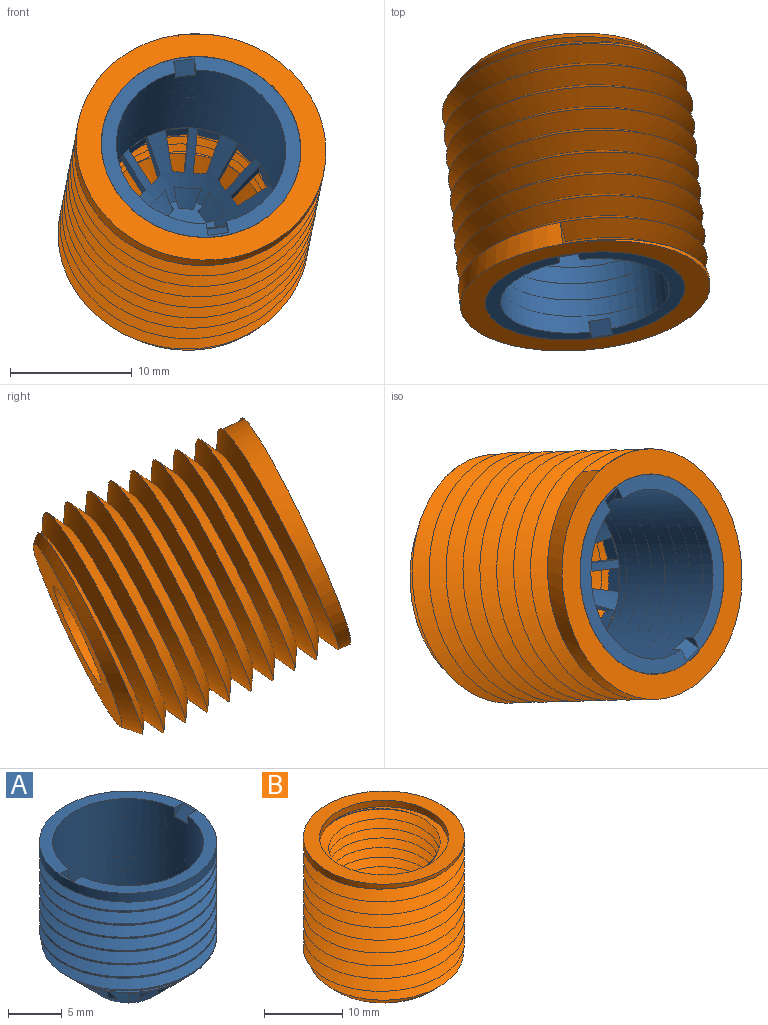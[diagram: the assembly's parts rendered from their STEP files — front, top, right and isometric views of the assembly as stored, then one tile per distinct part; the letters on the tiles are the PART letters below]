
ASSEMBLY  parts=2 mates=1
PART A: 152 faces, bbox 17.6x20.2x19.9 mm
  f0: cylinder r=7mm len=14mm, axis (0,0,1), area 481.2mm2, adj f1,f3,f4,f6,f7,f65,f66,f67
  f1: plane 1.75x0.06mm, normal (0,0,1), area 0mm2, adj f0,f2,f3,f151
  f2: plane 1.75x1mm, normal (0.71,0,0.71), area 2.5mm2, adj f1,f3,f150,f151
  f3: plane 1.06x1mm, normal (0,1,0), area 0.6mm2, adj f0,f1,f2,f150
  f4: plane 1.06x1mm, normal (0,1,0), area 0.6mm2, adj f0,f5,f148,f150
  f5: plane 1.75x1mm, normal (-0.71,0,0.71), area 2.5mm2, adj f4,f148,f149,f150
  f6: cone r=7mm half-angle=45deg, axis (0,0,1), area 0mm2, adj f0,f7
  f7: plane 2.15x1.49mm, normal (-1,0.04,0), area 2.4mm2, adj f0,f6,f8,f65,f66,f146,f147
  f8: cone r=8.23mm half-angle=45deg, axis (0,0,1), area 142mm2, adj f7,f9,f10,f11,f12,f13,f14,f15
  f9: plane 1.54x0.95mm, normal (0.78,0.62,0), area 1.3mm2, adj f8,f133,f138,f145
  f10: plane 1.54x0.96mm, normal (0.78,0.62,0), area 1.3mm2, adj f8,f139,f144,f145
  f11: plane 1.54x0.95mm, normal (-0.78,0.62,0), area 1.3mm2, adj f8,f109,f114,f145
  f12: plane 1.54x1.16mm, normal (-0.97,-0.22,0), area 1.3mm2, adj f8,f103,f108,f145
  f13: plane 1.54x1.17mm, normal (-0.97,-0.22,0), area 1.3mm2, adj f8,f97,f102,f145
  f14: plane 1.54x1.19mm, normal (0,1,0), area 1.3mm2, adj f8,f127,f132,f145
  f15: plane 1.54x1.19mm, normal (0,1,0), area 1.3mm2, adj f8,f121,f126,f145
  f16: plane 1.54x0.96mm, normal (-0.78,0.62,0), area 1.3mm2, adj f8,f115,f120,f145
  f17: plane 1.54x1.08mm, normal (0.43,-0.9,0), area 1.3mm2, adj f8,f73,f78,f145
  f18: plane 1.54x1.08mm, normal (0.43,-0.9,0), area 1.3mm2, adj f8,f79,f84,f145
  f19: plane 1.54x1.16mm, normal (0.97,-0.22,0), area 1.3mm2, adj f8,f67,f72,f145
  f20: plane 1.54x1.08mm, normal (-0.43,-0.9,0), area 1.3mm2, adj f8,f91,f96,f145
  f21: plane 1.54x1.08mm, normal (-0.43,-0.9,0), area 1.3mm2, adj f8,f85,f90,f145
  f22: plane 1.57x1.41mm, normal (-0.99,0.12,0), area 1.2mm2, adj f8,f23,f24,f31,f32,f61
  f23: plane 1.09x0.52mm, normal (-0.43,-0.9,0), area 0.6mm2, adj f22,f24,f33,f61
  f24: plane 4.97x4.86mm, normal (0,0,1), area 12.5mm2, adj f22,f23,f25,f26,f27,f28,f29,f30
  f25: plane 1.17x0.48mm, normal (-0.97,-0.22,0), area 0.6mm2, adj f24,f34,f36,f61
  f26: plane 0.94x0.75mm, normal (-0.78,0.62,0), area 0.6mm2, adj f24,f37,f39,f61
  f27: plane 1.2x0.48mm, normal (0,1,0), area 0.6mm2, adj f24,f40,f42,f61
  f28: plane 0.94x0.75mm, normal (0.78,0.62,0), area 0.6mm2, adj f24,f43,f45,f61
  f29: plane 1.17x0.48mm, normal (0.97,-0.22,0), area 0.6mm2, adj f24,f46,f60,f61
  f30: plane 1.09x0.52mm, normal (0.43,-0.9,0), area 0.6mm2, adj f24,f61,f62,f64
  f31: cone r=7mm half-angle=45deg, axis (0,0,1), area 45.9mm2, adj f22,f24,f32,f33,f34,f35,f36,f37
  f32: plane 2.54x1.93mm, normal (0.43,0.9,0), area 2.7mm2, adj f8,f22,f31,f33
  f33: plane 1.41x1.12mm, normal (0.71,-0.7,0), area 1.2mm2, adj f8,f23,f24,f31,f32,f61
  f34: plane 1.41x1.34mm, normal (-0.53,0.85,0), area 1.2mm2, adj f8,f24,f25,f31,f35,f61
  f35: plane 2.7x1.93mm, normal (0.97,0.22,0), area 2.7mm2, adj f8,f31,f34,f36
  f36: plane 1.57x1.41mm, normal (-0.11,-0.99,0), area 1.2mm2, adj f8,f24,f25,f31,f35,f61
  f37: plane 1.49x1.41mm, normal (0.34,0.94,0), area 1.2mm2, adj f8,f24,f26,f31,f38,f61
  f38: plane 2.27x1.93mm, normal (0.78,-0.62,0), area 2.7mm2, adj f8,f31,f37,f39
  f39: plane 1.41x1.33mm, normal (-0.84,-0.54,0), area 1.2mm2, adj f8,f24,f26,f31,f38,f61
  f40: plane 1.49x1.41mm, normal (0.95,0.32,0), area 1.2mm2, adj f8,f24,f27,f31,f41,f61
  f41: plane 2.76x1.93mm, normal (0,-1,0), area 2.7mm2, adj f8,f31,f40,f42
  f42: plane 1.49x1.41mm, normal (-0.95,0.32,0), area 1.2mm2, adj f8,f24,f27,f31,f41,f61
  f43: plane 1.41x1.33mm, normal (0.84,-0.54,0), area 1.2mm2, adj f8,f24,f28,f31,f44,f61
  f44: plane 2.27x1.93mm, normal (-0.78,-0.62,0), area 2.7mm2, adj f8,f31,f43,f45
  f45: plane 1.49x1.41mm, normal (-0.34,0.94,0), area 1.2mm2, adj f8,f24,f28,f31,f44,f61
  f46: plane 1.57x1.41mm, normal (0.11,-0.99,0), area 1.2mm2, adj f8,f24,f29,f31,f59,f61
  f47: cylinder r=8.23mm len=14.47mm, axis (0,0,1), area 4.7mm2, adj f8,f48,f56,f57
  f48: cylinder r=8.23mm len=16.46mm, axis (0,0,1), area 8.6mm2, adj f47,f49,f56,f57
  f49: cylinder r=8.23mm len=16.46mm, axis (0,0,1), area 8.6mm2, adj f48,f50,f56,f57
  f50: cylinder r=8.23mm len=16.46mm, axis (0,0,1), area 8.6mm2, adj f49,f51,f56,f57
  f51: cylinder r=8.23mm len=16.46mm, axis (0,0,1), area 8.6mm2, adj f50,f52,f56,f57
  f52: cylinder r=8.23mm len=16.46mm, axis (0,0,1), area 8.6mm2, adj f51,f53,f56,f57
  f53: cylinder r=8.23mm len=16.46mm, axis (0,0,1), area 8.6mm2, adj f52,f54,f56,f57
  f54: cylinder r=8.23mm len=16.46mm, axis (0,0,1), area 54.6mm2, adj f53,f55,f56,f57,f150
  f55: plane 17.38x17.38mm, normal (0,0,-1), area 25.3mm2, adj f54,f56,f57
  f56: bspline ~19.24x16.66mm, area 308mm2, adj f8,f47,f48,f49,f50,f51,f52,f53
  f57: bspline ~19.24x16.66mm, area 129.4mm2, adj f8,f47,f48,f49,f50,f51,f52,f53
  f58: plane 1.54x1.17mm, normal (0.97,-0.22,0), area 1.3mm2, adj f8,f66,f145,f146
  f59: plane 2.7x1.93mm, normal (-0.97,0.22,0), area 2.7mm2, adj f8,f31,f46,f60
  f60: plane 1.41x1.34mm, normal (0.53,0.85,0), area 1.2mm2, adj f8,f24,f29,f31,f59,f61
  f61: plane 6.42x6.29mm, normal (0,0,-1), area 16mm2, adj f8,f22,f23,f25,f26,f27,f28,f29
  f62: plane 1.41x1.12mm, normal (-0.71,-0.7,0), area 1.2mm2, adj f8,f24,f30,f31,f61,f63
  f63: plane 2.54x1.93mm, normal (-0.43,0.9,0), area 2.7mm2, adj f8,f31,f62,f64
  f64: plane 1.57x1.41mm, normal (0.99,0.12,0), area 1.2mm2, adj f8,f24,f30,f31,f61,f63
  f65: plane 0.03x0.01mm, normal (0,0,-1), area 0mm2, adj f0,f7,f66
  f66: plane 4.07x2.78mm, normal (0.22,0.97,0), area 3.4mm2, adj f0,f7,f8,f58,f65,f145
  f67: plane 4.07x2.78mm, normal (-0.22,-0.97,0), area 3.4mm2, adj f0,f8,f19,f68,f70,f145
  f68: plane 0.03x0.01mm, normal (0,0,-1), area 0mm2, adj f0,f67,f70
  f69: cone r=7mm half-angle=45deg, axis (0,0,1), area 0mm2, adj f0,f70
  f70: plane 1.99x1.49mm, normal (-0.92,0.4,0), area 2.4mm2, adj f0,f8,f67,f68,f69,f71,f72
  f71: plane 0.05x0.03mm, normal (0,0,-1), area 0mm2, adj f0,f70,f72
  f72: plane 3.8x2.19mm, normal (0.53,0.85,0), area 3.1mm2, adj f0,f8,f19,f70,f71,f145
  f73: plane 3.8x1.83mm, normal (-0.71,-0.7,0), area 3.1mm2, adj f0,f8,f17,f74,f76,f145
  f74: plane 0.04x0.04mm, normal (0,0,-1), area 0mm2, adj f0,f73,f76
  f75: cone r=7mm half-angle=45deg, axis (0,0,1), area 0mm2, adj f0,f76
  f76: plane 1.77x1.49mm, normal (-0.6,0.8,0), area 2.4mm2, adj f0,f8,f73,f74,f75,f77,f78
  f77: plane 0.03x0.02mm, normal (0,0,-1), area 0mm2, adj f0,f76,f78
  f78: plane 4.07x2.58mm, normal (0.9,0.43,0), area 3.4mm2, adj f0,f8,f17,f76,f77,f145
  f79: plane 4.07x2.58mm, normal (-0.9,-0.43,0), area 3.4mm2, adj f0,f8,f18,f80,f82,f145
  f80: plane 0.03x0.01mm, normal (0,0,-1), area 0mm2, adj f0,f79,f82
  f81: cone r=7mm half-angle=45deg, axis (0,0,1), area 0mm2, adj f0,f82
  f82: plane 2.09x1.49mm, normal (-0.26,0.97,0), area 2.4mm2, adj f0,f8,f79,f80,f81,f83,f84
  f83: plane 0.05x0.01mm, normal (0,0,-1), area 0mm2, adj f0,f82,f84
  f84: plane 3.8x2.56mm, normal (0.99,0.12,0), area 3.1mm2, adj f0,f8,f18,f82,f83,f145
  f85: plane 3.8x2.56mm, normal (-0.99,0.12,0), area 3.1mm2, adj f0,f8,f21,f86,f88,f145
  f86: plane 0.05x0.01mm, normal (0,0,-1), area 0mm2, adj f0,f85,f88
  f87: cone r=7mm half-angle=45deg, axis (0,0,1), area 0mm2, adj f0,f88
  f88: plane 2.09x1.49mm, normal (0.26,0.97,0), area 2.4mm2, adj f0,f8,f85,f86,f87,f89,f90
  f89: plane 0.03x0.01mm, normal (0,0,-1), area 0mm2, adj f0,f88,f90
  f90: plane 4.07x2.58mm, normal (0.9,-0.43,0), area 3.4mm2, adj f0,f8,f21,f88,f89,f145
  f91: plane 4.07x2.58mm, normal (-0.9,0.43,0), area 3.4mm2, adj f0,f8,f20,f92,f94,f145
  f92: plane 0.03x0.02mm, normal (0,0,-1), area 0mm2, adj f0,f91,f94
  f93: cone r=7mm half-angle=45deg, axis (0,0,1), area 0mm2, adj f0,f94
  f94: plane 1.77x1.49mm, normal (0.6,0.8,0), area 2.4mm2, adj f0,f8,f91,f92,f93,f95,f96
  f95: plane 0.04x0.04mm, normal (0,0,-1), area 0mm2, adj f0,f94,f96
  f96: plane 3.8x1.83mm, normal (0.71,-0.7,0), area 3.1mm2, adj f0,f8,f20,f94,f95,f145
  f97: plane 3.8x2.19mm, normal (-0.53,0.85,0), area 3.1mm2, adj f0,f8,f13,f98,f100,f145
  f98: plane 0.05x0.03mm, normal (0,0,-1), area 0mm2, adj f0,f97,f100
  f99: cone r=7mm half-angle=45deg, axis (0,0,1), area 0mm2, adj f0,f100
  f100: plane 1.99x1.49mm, normal (0.92,0.4,0), area 2.4mm2, adj f0,f8,f97,f98,f99,f101,f102
  f101: plane 0.03x0.01mm, normal (0,0,-1), area 0mm2, adj f0,f100,f102
  f102: plane 4.07x2.78mm, normal (0.22,-0.97,0), area 3.4mm2, adj f0,f8,f13,f100,f101,f145
  f103: plane 4.07x2.78mm, normal (-0.22,0.97,0), area 3.4mm2, adj f0,f8,f12,f104,f106,f145
  f104: plane 0.03x0.01mm, normal (0,0,-1), area 0mm2, adj f0,f103,f106
  f105: cone r=7mm half-angle=45deg, axis (0,0,1), area 0mm2, adj f0,f106
  f106: plane 2.15x1.49mm, normal (1,0.04,0), area 2.4mm2, adj f0,f8,f103,f104,f105,f107,f108
  f107: plane 0.05x0.01mm, normal (0,0,-1), area 0mm2, adj f0,f106,f108
  f108: plane 3.8x2.56mm, normal (-0.11,-0.99,0), area 3.1mm2, adj f0,f8,f12,f106,f107,f145
  f109: plane 3.8x2.43mm, normal (0.34,0.94,0), area 3.1mm2, adj f0,f8,f11,f110,f112,f145
  f110: plane 0.05x0.03mm, normal (0,0,-1), area 0mm2, adj f0,f109,f112
  f111: cone r=7mm half-angle=45deg, axis (0,0,1), area 0mm2, adj f0,f112
  f112: plane 1.93x1.49mm, normal (0.89,-0.47,0), area 2.4mm2, adj f0,f8,f109,f110,f111,f113,f114
  f113: plane 0.03x0.02mm, normal (0,0,-1), area 0mm2, adj f0,f112,f114
  f114: plane 4.07x2.24mm, normal (-0.62,-0.78,0), area 3.4mm2, adj f0,f8,f11,f112,f113,f145
  f115: plane 4.07x2.24mm, normal (0.62,0.78,0), area 3.4mm2, adj f0,f8,f16,f116,f118,f145
  f116: plane 0.03x0.03mm, normal (0,0,-1), area 0mm2, adj f0,f115,f118
  f117: cone r=7mm half-angle=45deg, axis (0,0,1), area 0mm2, adj f0,f118
  f118: plane 1.68x1.49mm, normal (0.65,-0.76,0), area 2.4mm2, adj f0,f8,f115,f116,f117,f119,f120
  f119: plane 0.04x0.04mm, normal (0,0,-1), area 0mm2, adj f0,f118,f120
  f120: plane 3.8x2.17mm, normal (-0.84,-0.54,0), area 3.1mm2, adj f0,f8,f16,f118,f119,f145
  f121: plane 3.8x2.44mm, normal (0.95,0.32,0), area 3.1mm2, adj f0,f8,f15,f122,f124,f145
  f122: plane 0.05x0.02mm, normal (0,0,-1), area 0mm2, adj f0,f121,f124
  f123: cone r=7mm half-angle=45deg, axis (0,0,1), area 0mm2, adj f0,f124
  f124: plane 2.12x1.49mm, normal (0.19,-0.98,0), area 2.4mm2, adj f0,f8,f121,f122,f123,f125,f126
  f125: plane 0.03x0.01mm, normal (0,0,-1), area 0mm2, adj f0,f124,f126
  f126: plane 4.07x2.85mm, normal (-1,0,0), area 3.4mm2, adj f0,f8,f15,f124,f125,f145
  f127: plane 4.07x2.85mm, normal (1,0,0), area 3.4mm2, adj f0,f8,f14,f128,f130,f145
  f128: plane 0.03x0.01mm, normal (0,0,-1), area 0mm2, adj f0,f127,f130
  f129: cone r=7mm half-angle=45deg, axis (0,0,1), area 0mm2, adj f0,f130
  f130: plane 2.12x1.49mm, normal (-0.19,-0.98,0), area 2.4mm2, adj f0,f8,f127,f128,f129,f131,f132
  f131: plane 0.05x0.02mm, normal (0,0,-1), area 0mm2, adj f0,f130,f132
  f132: plane 3.8x2.44mm, normal (-0.95,0.32,0), area 3.1mm2, adj f0,f8,f14,f130,f131,f145
  f133: plane 3.8x2.17mm, normal (0.84,-0.54,0), area 3.1mm2, adj f0,f8,f9,f134,f136,f145
  f134: plane 0.04x0.04mm, normal (0,0,-1), area 0mm2, adj f0,f133,f136
  f135: cone r=7mm half-angle=45deg, axis (0,0,1), area 0mm2, adj f0,f136
  f136: plane 1.68x1.49mm, normal (-0.65,-0.76,0), area 2.4mm2, adj f0,f8,f133,f134,f135,f137,f138
  f137: plane 0.03x0.03mm, normal (0,0,-1), area 0mm2, adj f0,f136,f138
  f138: plane 4.07x2.24mm, normal (-0.62,0.78,0), area 3.4mm2, adj f0,f8,f9,f136,f137,f145
  f139: plane 4.07x2.24mm, normal (0.62,-0.78,0), area 3.4mm2, adj f0,f8,f10,f140,f142,f145
  f140: plane 0.03x0.02mm, normal (0,0,-1), area 0mm2, adj f0,f139,f142
  f141: cone r=7mm half-angle=45deg, axis (0,0,1), area 0mm2, adj f0,f142
  f142: plane 1.93x1.49mm, normal (-0.89,-0.47,0), area 2.4mm2, adj f0,f8,f139,f140,f141,f143,f144
  f143: plane 0.05x0.03mm, normal (0,0,-1), area 0mm2, adj f0,f142,f144
  f144: plane 3.8x2.43mm, normal (-0.34,0.94,0), area 3.1mm2, adj f0,f8,f10,f142,f143,f145
  f145: cone r=7mm half-angle=45deg, axis (0,0,1), area 137.8mm2, adj f0,f9,f10,f11,f12,f13,f14,f15
  f146: plane 3.8x2.56mm, normal (0.11,-0.99,0), area 3.1mm2, adj f0,f7,f8,f58,f145,f147
  f147: plane 0.05x0.01mm, normal (0,0,-1), area 0mm2, adj f0,f7,f146
  f148: plane 1.75x0.06mm, normal (0,0,1), area 0mm2, adj f0,f4,f5,f149
  f149: plane 1.06x1mm, normal (0,-1,0), area 0.6mm2, adj f0,f5,f148,f150
  f150: plane 16.46x16.46mm, normal (0,0,1), area 55.3mm2, adj f0,f2,f3,f4,f5,f54,f149,f151
  f151: plane 1.06x1mm, normal (0,-1,0), area 0.6mm2, adj f0,f1,f2,f150
PART B: 26 faces, bbox 21.6x24.8x22 mm
  f0: cylinder r=10.32mm len=20.64mm, axis (0,0,-1), area 65.3mm2, adj f1,f2,f3
  f1: plane 20.64x20.64mm, normal (0,0,1), area 120.8mm2, adj f0,f9
  f2: plane 2x1.74mm, normal (0,-1,0), area 1.7mm2, adj f0,f3,f4,f5
  f3: bspline ~23.84x20.64mm, area 0.3mm2, adj f0,f2,f4
  f4: bspline ~23.82x20.63mm, area 1093.3mm2, adj f2,f3,f5,f7,f8
  f5: bspline ~23.82x20.63mm, area 1031.2mm2, adj f2,f4,f7,f8
  f6: plane 16.64x16.64mm, normal (0,0,-1), area 153.9mm2, adj f7,f25
  f7: cone r=10.32mm half-angle=45deg, axis (0,0,1), area 90.3mm2, adj f4,f5,f6,f8
  f8: cone r=10.32mm half-angle=45deg, axis (0,0,1), area 0mm2, adj f4,f5,f7
  f9: cylinder r=8.25mm len=16.5mm, axis (0,0,1), area 54.4mm2, adj f1,f10,f21,f22,f24
  f10: cylinder r=8.25mm len=16.5mm, axis (0,0,1), area 7.4mm2, adj f9,f11,f21,f22
  f11: cylinder r=8.25mm len=16.5mm, axis (0,0,1), area 7.5mm2, adj f10,f12,f21,f22
  f12: cylinder r=8.25mm len=16.5mm, axis (0,0,1), area 7.5mm2, adj f11,f13,f21,f22
  f13: cylinder r=8.25mm len=16.5mm, axis (0,0,1), area 7.5mm2, adj f12,f14,f21,f22
  f14: cylinder r=8.25mm len=16.5mm, axis (0,0,1), area 7.5mm2, adj f13,f15,f21,f22
  f15: cylinder r=8.25mm len=16.5mm, axis (0,0,1), area 7.5mm2, adj f14,f16,f21,f22
  f16: cylinder r=8.25mm len=16.5mm, axis (0,0,1), area 7.4mm2, adj f15,f17,f21,f22
  f17: cylinder r=8.25mm len=16.5mm, axis (0,0,1), area 7.4mm2, adj f16,f18,f21,f22
  f18: cylinder r=8.25mm len=16.5mm, axis (0,0,1), area 7.4mm2, adj f17,f19,f21,f22
  f19: cylinder r=8.25mm len=16.5mm, axis (0,0,1), area 44.9mm2, adj f18,f20,f21,f22,f23
  f20: plane 16.5x16.5mm, normal (0,0,1), area 37.1mm2, adj f19,f25
  f21: bspline ~19.24x16.73mm, area 706.5mm2, adj f9,f10,f11,f12,f13,f14,f15,f16
  f22: bspline ~19.24x16.66mm, area 676mm2, adj f9,f10,f11,f12,f13,f14,f15,f16
  f23: plane 1.45x1.11mm, normal (-0.87,0.5,0), area 0.8mm2, adj f19,f21,f22
  f24: plane 17.44x17.44mm, normal (0,0,1), area 26.2mm2, adj f9,f21,f22
  f25: cone r=4.5mm half-angle=45deg, axis (0,0,1), area 159.9mm2, adj f6,f20
PLACE A rot(axis=(0.43,-0.45,0.78),116.9deg) t=(-70.13,-180.04,-13.07)mm
PLACE B rot(axis=(0.43,-0.45,0.78),116.9deg) t=(-70.13,-180.04,-13.07)mm
MATE cylindrical B.f9 <-> A.f8  axis (0.09,-0.9,0.43) through (-68.42,-198.02,-4.48)mm
